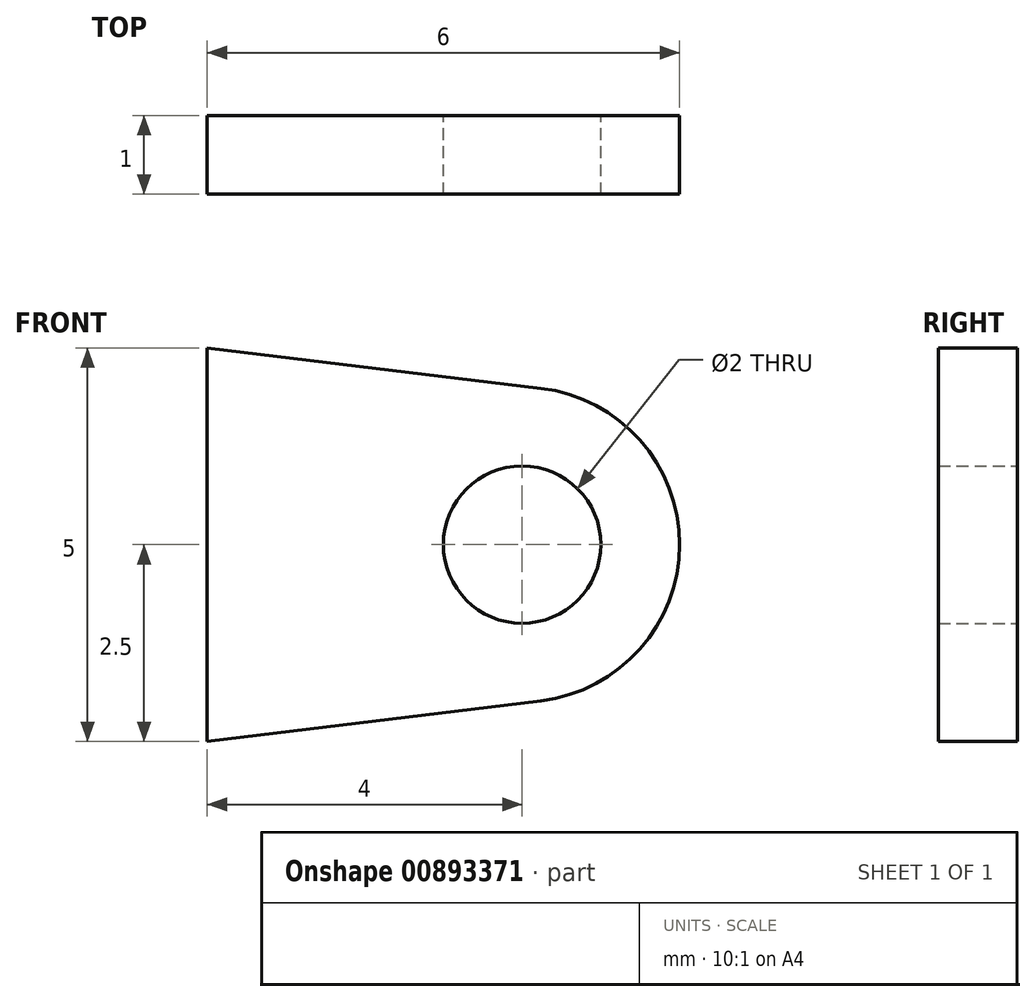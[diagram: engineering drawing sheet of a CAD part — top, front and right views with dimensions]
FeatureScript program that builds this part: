
annotation { "Feature Type Name" : "Feature", "Feature Type Description" : "" }
export const myFeature = defineFeature(function(context is Context, id is Id, definition is map)
    precondition{}
    {
        {
            var Q0;
            Q0=qCreatedBy(makeId("Front.planeOp"),FACE);
            var sketch = newSketch(context, id + "F0", { "sketchPlane" : qUnion([Q0])});
            skCircle(sketch, "E0", {"center": v(0, 0) * mm, "radius": 1 * mm});
            skArc(sketch, "E1", {"start": v(0.24, -1.99) * mm, "mid": v(2, 0) * mm, "end": v(0.24, 1.99) * mm});
            skLineSegment(sketch, "E2", {"start": v(-4, 2.5) * mm, "end": v(-4, -2.5) * mm});
            skPoint(sketch, "E3.start.orphan", {"position": v(-16.68, 0) * mm});
            skLineSegment(sketch, "E4", {"start": v(-4, 2.5) * mm, "end": v(0.24, 1.99) * mm});
            skLineSegment(sketch, "E5", {"start": v(-4, -2.5) * mm, "end": v(0.24, -1.99) * mm});
            skSolve(sketch);
        }
        {
            var Q0;
            Q0=makeQuery(id+"F0.imprint","IMPRINT",FACE,{"disambiguationData":[TD([[makeQuery(id+"F0.imprint","IMPRINT",EDGE,{"derivedFrom":sQuery(id+"F0.wireOp",EDGE,"E0")}),-1.0]])]});
            extrude(context, id + "F1", {"entities" : qUnion([Q0]), "depth" : 1 * mm, "offsetDistance" : 25 * mm});
        }
    });
